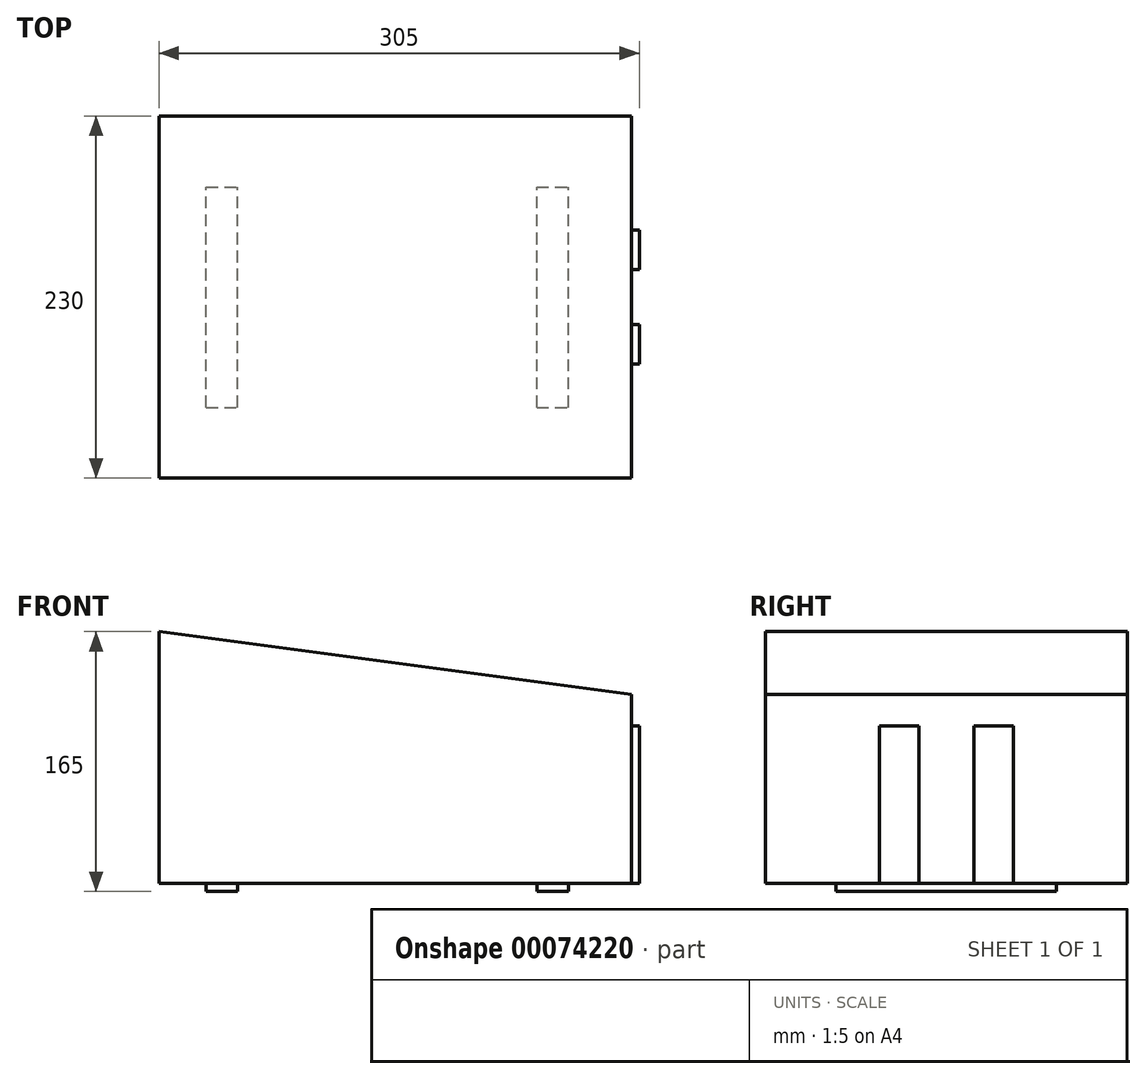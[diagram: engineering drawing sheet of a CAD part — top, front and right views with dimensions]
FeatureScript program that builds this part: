
annotation { "Feature Type Name" : "Feature", "Feature Type Description" : "" }
export const myFeature = defineFeature(function(context is Context, id is Id, definition is map)
    precondition{}
    {
        {
            var Q0;
            Q0=qCreatedBy(makeId("Front.planeOp"),FACE);
            var sketch = newSketch(context, id + "F0", { "sketchPlane" : qUnion([Q0])});
            skLineSegment(sketch, "E0", {"start": v(0, 0) * mm, "end": v(0, 120) * mm});
            skLineSegment(sketch, "E1", {"start": v(0, 120) * mm, "end": v(-300, 160) * mm});
            skLineSegment(sketch, "E2", {"start": v(-300, 160) * mm, "end": v(-300, 0) * mm});
            skLineSegment(sketch, "E3", {"start": v(-300, 0) * mm, "end": v(0, 0) * mm});
            skSolve(sketch);
        }
        {
            var Q0;
            Q0=makeQuery(id+"F0.imprint","IMPRINT",FACE,{"disambiguationData":[TD([[makeQuery(id+"F0.imprint","IMPRINT",EDGE,{"derivedFrom":sQuery(id+"F0.wireOp",EDGE,"E0")}),1.0]])]});
            extrude(context, id + "F1", {"entities" : qUnion([Q0]), "endBound" : BoundingType.SYMMETRIC, "depth" : 230 * mm});
        }
        {
            var Q0;
            Q0=qCreatedBy(makeId("Top.planeOp"),FACE);
            var sketch = newSketch(context, id + "F2", { "sketchPlane" : qUnion([Q0])});
            skLineSegment(sketch, "E4.bottom", {"start": v(-270, -70) * mm, "end": v(-250, -70) * mm});
            skLineSegment(sketch, "E4.top", {"start": v(-270, 70) * mm, "end": v(-250, 70) * mm});
            skLineSegment(sketch, "E4.left", {"start": v(-270, -70) * mm, "end": v(-270, 70) * mm});
            skLineSegment(sketch, "E4.right", {"start": v(-250, -70) * mm, "end": v(-250, 70) * mm});
            skLineSegment(sketch, "E5.bottom", {"start": v(-60, -70) * mm, "end": v(-40, -70) * mm});
            skLineSegment(sketch, "E5.top", {"start": v(-60, 70) * mm, "end": v(-40, 70) * mm});
            skLineSegment(sketch, "E5.left", {"start": v(-60, -70) * mm, "end": v(-60, 70) * mm});
            skLineSegment(sketch, "E5.right", {"start": v(-40, -70) * mm, "end": v(-40, 70) * mm});
            skLineSegment(sketch, "E6", {"start": v(0, 0) * mm, "end": v(-40, 0) * mm, "construction": true});
            skSolve(sketch);
        }
        {
            var Q0;
            Q0 = qSketchRegion(id + "F2", true);
            extrude(context, id + "F3", {"entities" : qUnion([Q0]), "operationType" : NewBodyOperationType.ADD, "oppositeDirection" : true, "depth" : 5 * mm});
        }
        {
            var Q0;
            Q0=qCreatedBy(makeId("Right.planeOp"),FACE);
            var sketch = newSketch(context, id + "F4", { "sketchPlane" : qUnion([Q0])});
            skLineSegment(sketch, "E7.bottom", {"start": v(17.5, 0) * mm, "end": v(42.5, 0) * mm});
            skLineSegment(sketch, "E7.top", {"start": v(17.5, 100) * mm, "end": v(42.5, 100) * mm});
            skLineSegment(sketch, "E7.left", {"start": v(17.5, 0) * mm, "end": v(17.5, 100) * mm});
            skLineSegment(sketch, "E7.right", {"start": v(42.5, 0) * mm, "end": v(42.5, 100) * mm});
            skLineSegment(sketch, "E8", {"start": v(0, 0) * mm, "end": v(0, 63.54) * mm, "construction": true});
            skLineSegment(sketch, "E9.MirrorCS", {"start": v(-17.5, 0) * mm, "end": v(-42.5, 0) * mm});
            skLineSegment(sketch, "E10.MirrorCS", {"start": v(-17.5, 100) * mm, "end": v(-42.5, 100) * mm});
            skLineSegment(sketch, "E11.MirrorCS", {"start": v(-17.5, 0) * mm, "end": v(-17.5, 100) * mm});
            skLineSegment(sketch, "E12.MirrorCS", {"start": v(-42.5, 0) * mm, "end": v(-42.5, 100) * mm});
            skSolve(sketch);
        }
        {
            var Q0;
            Q0 = qSketchRegion(id + "F4", true);
            extrude(context, id + "F5", {"entities" : qUnion([Q0]), "operationType" : NewBodyOperationType.ADD, "depth" : 5 * mm});
        }
    });
